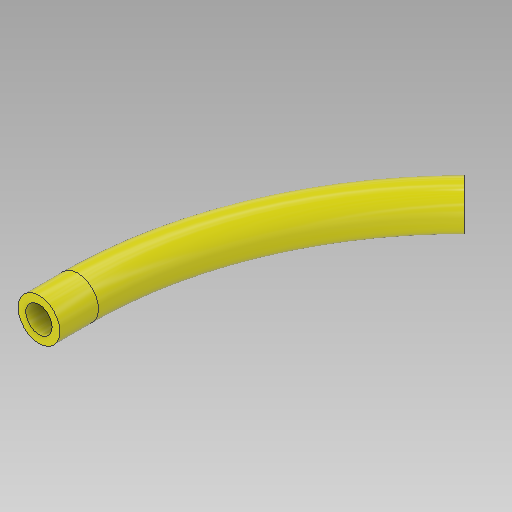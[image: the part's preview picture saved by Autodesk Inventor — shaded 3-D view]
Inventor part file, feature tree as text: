
AUTODESK INVENTOR PART (.ipt)
format: ipt  version: 2018.1 (Build 221171000, 171)  size: 142,848 bytes
history: native  units: in
note: dims shown in document units (in); Inventor stores cm internally (conversion verified against a paired STEP export)
features: sketch x3, extrude x1, sweep x1, projected_geometry x1
ambient origin geometry x8: Origin, YZ Plane, XZ Plane, XY Plane, X Axis, Y Axis, Z Axis, Center Point
bodies: Solid1 (feature_tree)
feature tree (6):
  extrude  "Extrusion1"  Depth=0.0394in
  sweep  "Sweep1"
  sketch  "Sketch1"  dims[d0=0.1339in d1=0.0394in]
  sketch  "Sketch2"  dims[d2=0.1969in d3=0.0in d6=1.5066in]
  sketch  "Sketch3"  dims[d7=0.0in d8=0.0in]
  projected_geometry  "Projected Loop1"
